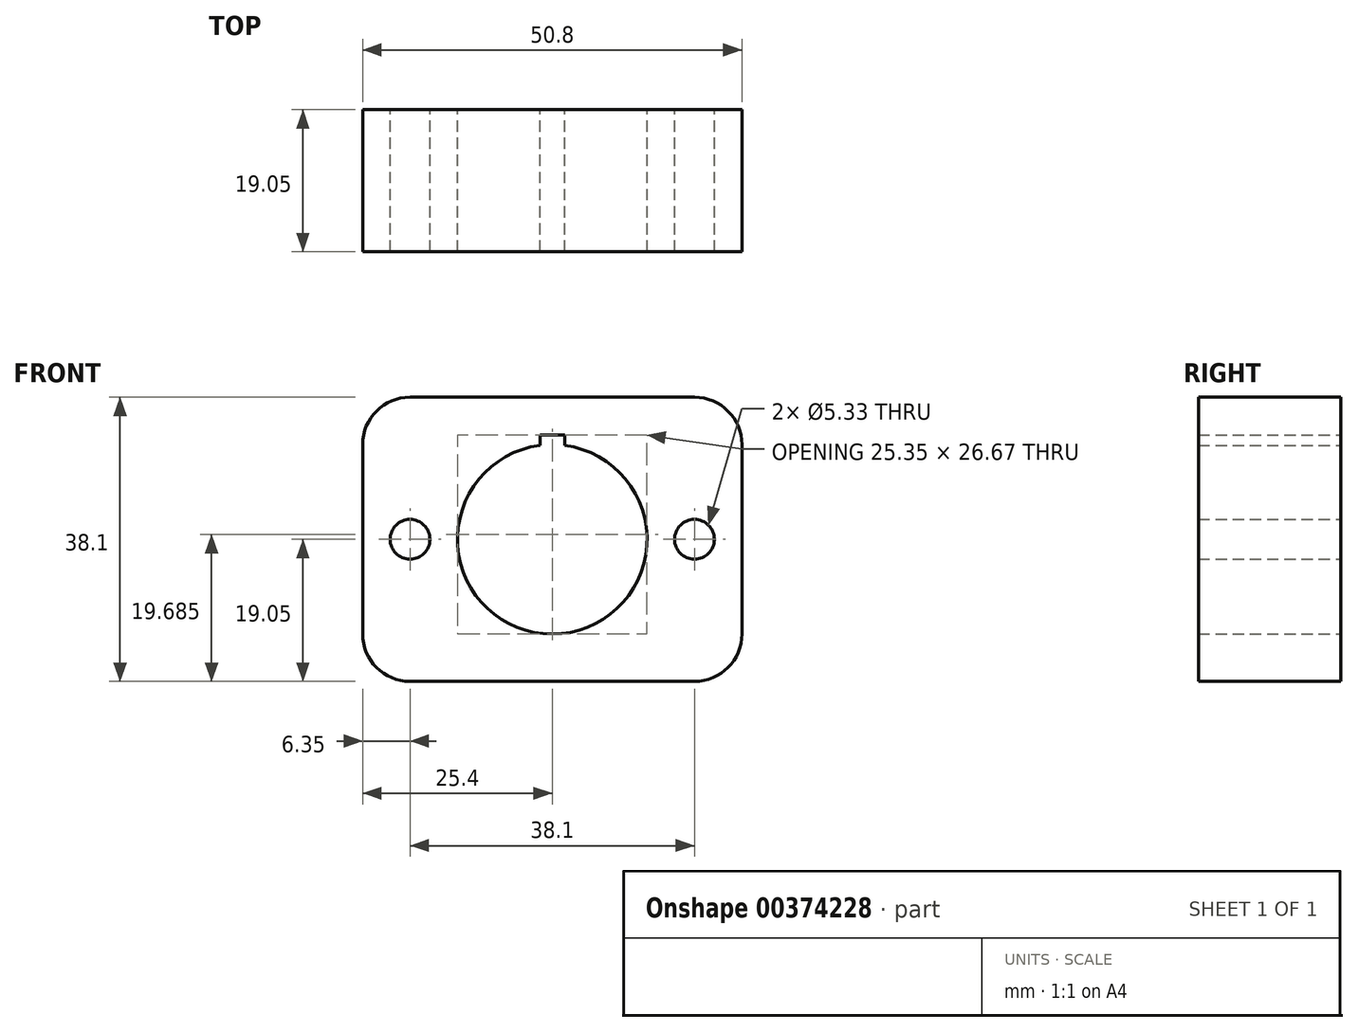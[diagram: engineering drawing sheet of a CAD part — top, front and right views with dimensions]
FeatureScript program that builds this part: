
annotation { "Feature Type Name" : "Feature", "Feature Type Description" : "" }
export const myFeature = defineFeature(function(context is Context, id is Id, definition is map)
    precondition{}
    {
        {
            var Q0;
            Q0=qCreatedBy(makeId("Front.planeOp"),FACE);
            var sketch = newSketch(context, id + "F0", { "sketchPlane" : qUnion([Q0])});
            skLineSegment(sketch, "E0.bottom", {"start": v(-19.05, 19.05) * mm, "end": v(19.05, 19.05) * mm});
            skLineSegment(sketch, "E0.top", {"start": v(-19.05, -19.05) * mm, "end": v(19.05, -19.05) * mm});
            skLineSegment(sketch, "E0.left", {"start": v(-25.4, 12.7) * mm, "end": v(-25.4, -12.7) * mm});
            skLineSegment(sketch, "E0.right", {"start": v(25.4, 12.7) * mm, "end": v(25.4, -12.7) * mm});
            skPoint(sketch, "E0.middle", {"position": v(0, 0) * mm});
            skLineSegment(sketch, "E1", {"start": v(0, -36.25) * mm, "end": v(0, 48.66) * mm, "construction": true});
            skPoint(sketch, "E2.visualSharp", {"position": v(-25.4, 19.05) * mm});
            skArc(sketch, "E2.filletArc", {"start": v(-19.05, 19.05) * mm, "mid": v(-23.54, 17.2) * mm, "end": v(-25.4, 12.7) * mm});
            skPoint(sketch, "E3.visualSharp", {"position": v(-25.4, -19.05) * mm});
            skArc(sketch, "E3.filletArc", {"start": v(-25.4, -12.7) * mm, "mid": v(-23.54, -17.2) * mm, "end": v(-19.05, -19.05) * mm});
            skPoint(sketch, "E4.visualSharp", {"position": v(25.4, 19.05) * mm});
            skArc(sketch, "E4.filletArc", {"start": v(25.4, 12.7) * mm, "mid": v(23.54, 17.2) * mm, "end": v(19.05, 19.05) * mm});
            skPoint(sketch, "E5.visualSharp", {"position": v(25.4, -19.05) * mm});
            skArc(sketch, "E5.filletArc", {"start": v(19.05, -19.05) * mm, "mid": v(23.54, -17.2) * mm, "end": v(25.4, -12.7) * mm});
            skCircle(sketch, "E6", {"center": v(0, 0) * mm, "radius": 12.7 * mm});
            skCircle(sketch, "E7", {"center": v(-19.05, 0) * mm, "radius": 2.67 * mm});
            skCircle(sketch, "E8.MirrorC", {"center": v(19.05, 0) * mm, "radius": 2.67 * mm});
            skLineSegment(sketch, "E9.bottom", {"start": v(1.65, 11.43) * mm, "end": v(-1.65, 11.43) * mm});
            skLineSegment(sketch, "E9.top", {"start": v(1.65, 13.97) * mm, "end": v(-1.65, 13.97) * mm});
            skLineSegment(sketch, "E9.left", {"start": v(1.65, 11.43) * mm, "end": v(1.65, 13.97) * mm});
            skLineSegment(sketch, "E9.right", {"start": v(-1.65, 11.43) * mm, "end": v(-1.65, 13.97) * mm});
            skPoint(sketch, "E9.middle", {"position": v(0, 12.7) * mm});
            skSolve(sketch);
        }
        {
            var Q0;
            Q0=makeQuery(id+"F0.imprint","IMPRINT",FACE,{"disambiguationData":[TD([[makeQuery(id+"F0.imprint","IMPRINT",EDGE,{"derivedFrom":sQuery(id+"F0.wireOp",EDGE,"E0.bottom")}),-1.0]])]});
            extrude(context, id + "F1", {"entities" : qUnion([Q0]), "depth" : 19.05 * mm});
        }
        {
            var Q0;
            Q0=makeQuery(id+"F0.imprint","IMPRINT",FACE,{"disambiguationData":[TD([[makeQuery(id+"F0.imprint","IMPRINT",EDGE,{"derivedFrom":sQuery(id+"F0.wireOp",EDGE,"E0.bottom")}),-1.0]])]});
            extrude(context, id + "F2", {"entities" : qUnion([Q0]), "operationType" : NewBodyOperationType.ADD, "depth" : 19.05 * mm});
        }
    });
